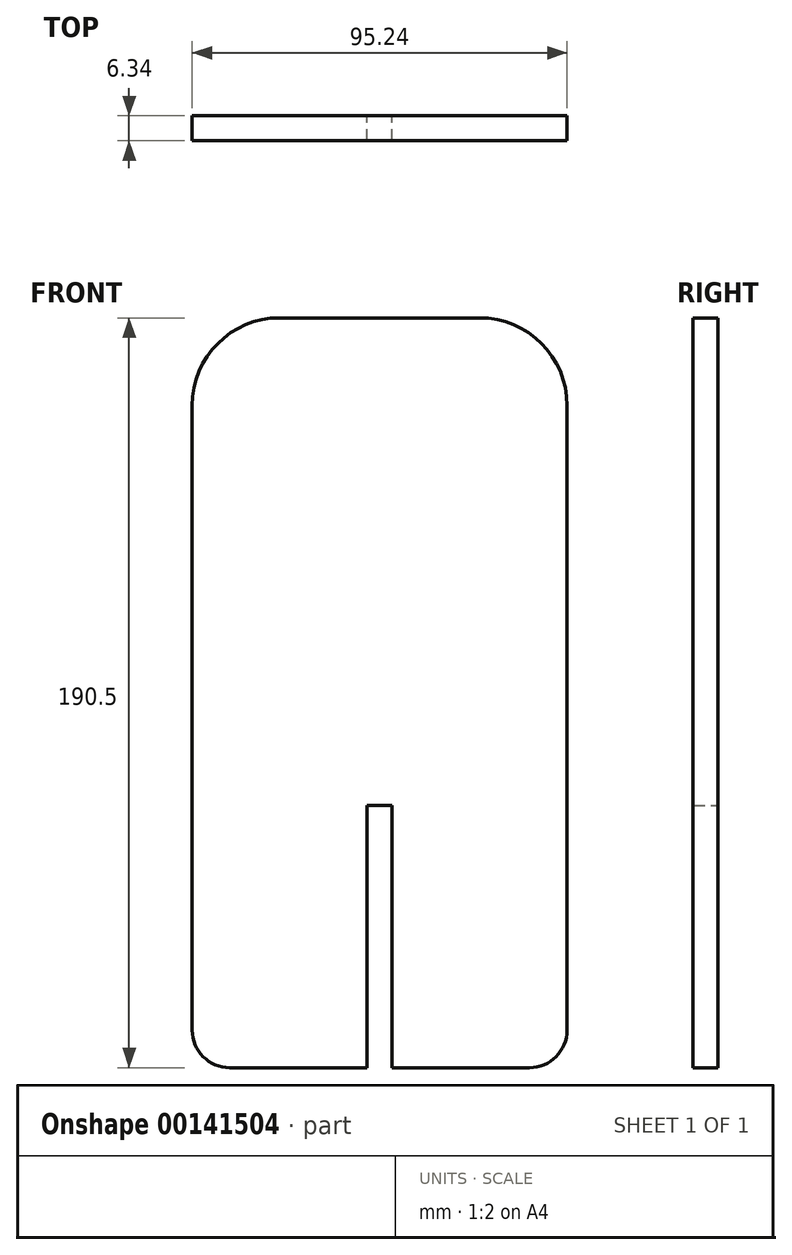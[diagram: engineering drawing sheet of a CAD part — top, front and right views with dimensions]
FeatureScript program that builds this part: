
annotation { "Feature Type Name" : "Feature", "Feature Type Description" : "" }
export const myFeature = defineFeature(function(context is Context, id is Id, definition is map)
    precondition{}
    {
        {
            var Q0;
            Q0=qCreatedBy(makeId("Front.planeOp"),FACE);
            var sketch = newSketch(context, id + "F0", { "sketchPlane" : qUnion([Q0])});
            skLineSegment(sketch, "E0.bottom", {"start": v(-25.4, 82.37) * mm, "end": v(25.4, 82.37) * mm});
            skLineSegment(sketch, "E0.top", {"start": v(-38.1, -108.13) * mm, "end": v(-3.18, -108.13) * mm});
            skLineSegment(sketch, "E0.left", {"start": v(-47.63, 60.15) * mm, "end": v(-47.62, -98.6) * mm});
            skLineSegment(sketch, "E0.right", {"start": v(47.62, 60.15) * mm, "end": v(47.63, -98.6) * mm});
            skLineSegment(sketch, "E1", {"start": v(0, -41.45) * mm, "end": v(3.17, -41.45) * mm});
            skLineSegment(sketch, "E2", {"start": v(3.17, -41.45) * mm, "end": v(3.18, -108.13) * mm});
            skLineSegment(sketch, "E3.MirrorCS", {"start": v(0, -41.45) * mm, "end": v(-3.17, -41.45) * mm});
            skLineSegment(sketch, "E4.MirrorCS", {"start": v(-3.17, -41.45) * mm, "end": v(-3.18, -108.13) * mm});
            skLineSegment(sketch, "E5.trimOffspring", {"start": v(3.18, -108.13) * mm, "end": v(38.1, -108.13) * mm});
            skPoint(sketch, "E6.visualSharp", {"position": v(-47.63, 82.37) * mm});
            skArc(sketch, "E6.filletArc", {"start": v(-25.4, 82.37) * mm, "mid": v(-41.12, 75.86) * mm, "end": v(-47.63, 60.15) * mm});
            skPoint(sketch, "E7.visualSharp", {"position": v(47.62, 82.37) * mm});
            skArc(sketch, "E7.filletArc", {"start": v(47.62, 60.15) * mm, "mid": v(41.12, 75.86) * mm, "end": v(25.4, 82.37) * mm});
            skPoint(sketch, "E8.visualSharp", {"position": v(-47.62, -108.13) * mm});
            skArc(sketch, "E8.filletArc", {"start": v(-47.62, -98.6) * mm, "mid": v(-44.84, -105.34) * mm, "end": v(-38.1, -108.13) * mm});
            skPoint(sketch, "E9.visualSharp", {"position": v(47.63, -108.13) * mm});
            skArc(sketch, "E9.filletArc", {"start": v(38.1, -108.13) * mm, "mid": v(44.84, -105.34) * mm, "end": v(47.63, -98.6) * mm});
            skSolve(sketch);
        }
        {
            var Q0;
            Q0 = qSketchRegion(id + "F0", true);
            extrude(context, id + "F1", {"entities" : qUnion([Q0]), "endBound" : BoundingType.SYMMETRIC, "depth" : 6.35 * mm});
        }
    });
